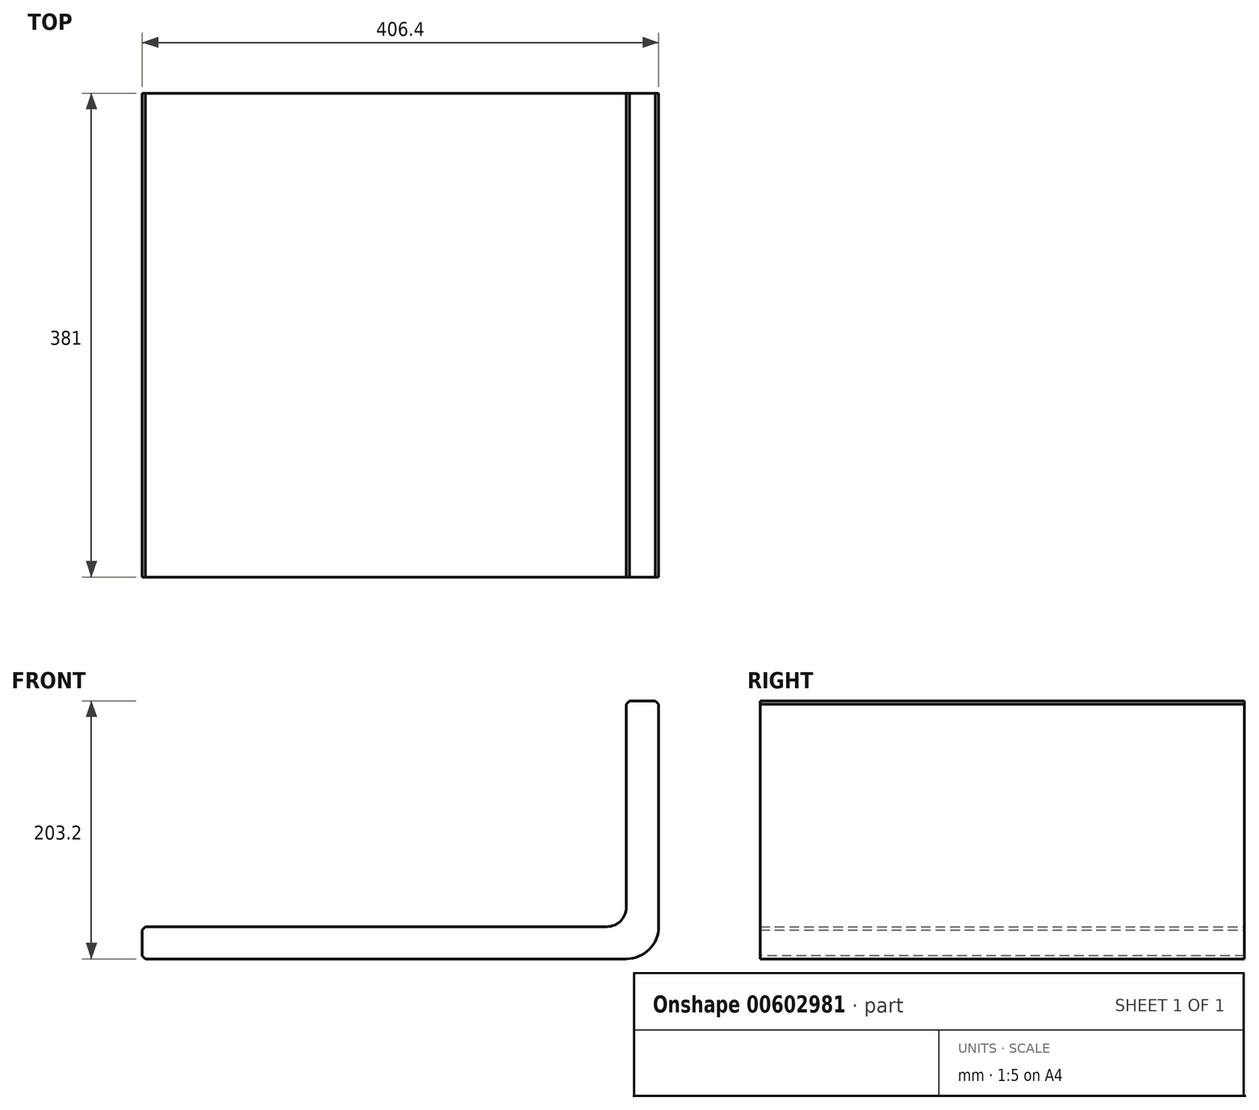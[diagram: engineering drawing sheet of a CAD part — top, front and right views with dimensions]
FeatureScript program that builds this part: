
annotation { "Feature Type Name" : "Feature", "Feature Type Description" : "" }
export const myFeature = defineFeature(function(context is Context, id is Id, definition is map)
    precondition{}
    {
        {
            var Q0;
            Q0=qCreatedBy(makeId("Front.planeOp"),FACE);
            var sketch = newSketch(context, id + "F0", { "sketchPlane" : qUnion([Q0])});
            skLineSegment(sketch, "E0.bottom", {"start": v(22.42, 25.4) * mm, "end": v(388.18, 25.4) * mm});
            skLineSegment(sketch, "E0.top", {"start": v(22.42, 0) * mm, "end": v(428.82, 0) * mm});
            skLineSegment(sketch, "E0.left", {"start": v(22.42, 25.4) * mm, "end": v(22.42, 0) * mm});
            skLineSegment(sketch, "E0.right", {"start": v(428.82, 25.4) * mm, "end": v(428.82, 0) * mm});
            skLineSegment(sketch, "E1.bottom", {"start": v(413.58, 0) * mm, "end": v(403.42, 0) * mm});
            skLineSegment(sketch, "E1.top", {"start": v(428.82, 203.2) * mm, "end": v(403.42, 203.2) * mm});
            skLineSegment(sketch, "E1.left", {"start": v(428.82, 25.4) * mm, "end": v(428.82, 203.2) * mm});
            skLineSegment(sketch, "E1.right", {"start": v(403.42, 40.64) * mm, "end": v(403.42, 203.2) * mm});
            skPoint(sketch, "E2.visualSharp", {"position": v(428.82, 0) * mm});
            skArc(sketch, "E2.filletArc", {"start": v(403.42, 0) * mm, "mid": v(421.38, 7.44) * mm, "end": v(428.82, 25.4) * mm});
            skArc(sketch, "E3.filletArc", {"start": v(388.18, 25.4) * mm, "mid": v(398.96, 29.86) * mm, "end": v(403.42, 40.64) * mm});
            skSolve(sketch);
        }
        {
            var Q0;
            Q0=makeQuery(id+"F0.imprint","IMPRINT",FACE,{"disambiguationData":[TD([[makeQuery(id+"F0.imprint","IMPRINT",EDGE,{"derivedFrom":sQuery(id+"F0.wireOp",EDGE,"E0.bottom")}),-1.0]])]});
            extrude(context, id + "F1", {"entities" : qUnion([Q0]), "depth" : 381 * mm, "offsetDistance" : 25.4 * mm});
        }
        {
            var Q0;
            Q0=makeQuery(id+"F1.opExtrude","SWEPT_EDGE",EDGE,{"disambiguationData":[OSD([sQuery(id+"F0.wireOp",EDGE,"E0.top"),sQuery(id+"F0.wireOp",EDGE,"E0.left")])]});
            var Q1;
            Q1=makeQuery(id+"F1.opExtrude","SWEPT_EDGE",EDGE,{"disambiguationData":[OSD([sQuery(id+"F0.wireOp",EDGE,"E0.bottom"),sQuery(id+"F0.wireOp",EDGE,"E0.left")])]});
            var Q2;
            Q2=makeQuery(id+"F1.opExtrude","SWEPT_EDGE",EDGE,{"disambiguationData":[OSD([sQuery(id+"F0.wireOp",EDGE,"E1.top"),sQuery(id+"F0.wireOp",EDGE,"E1.left")])]});
            var Q3;
            Q3=makeQuery(id+"F1.opExtrude","SWEPT_EDGE",EDGE,{"disambiguationData":[OSD([sQuery(id+"F0.wireOp",EDGE,"E1.top"),sQuery(id+"F0.wireOp",EDGE,"E1.right")])]});
            chamfer(context, id + "F2", {"entities" : qUnion([Q0, Q1, Q2, Q3]), "width" : 2.54 * mm, "tangentPropagation" : true});
        }
    });
